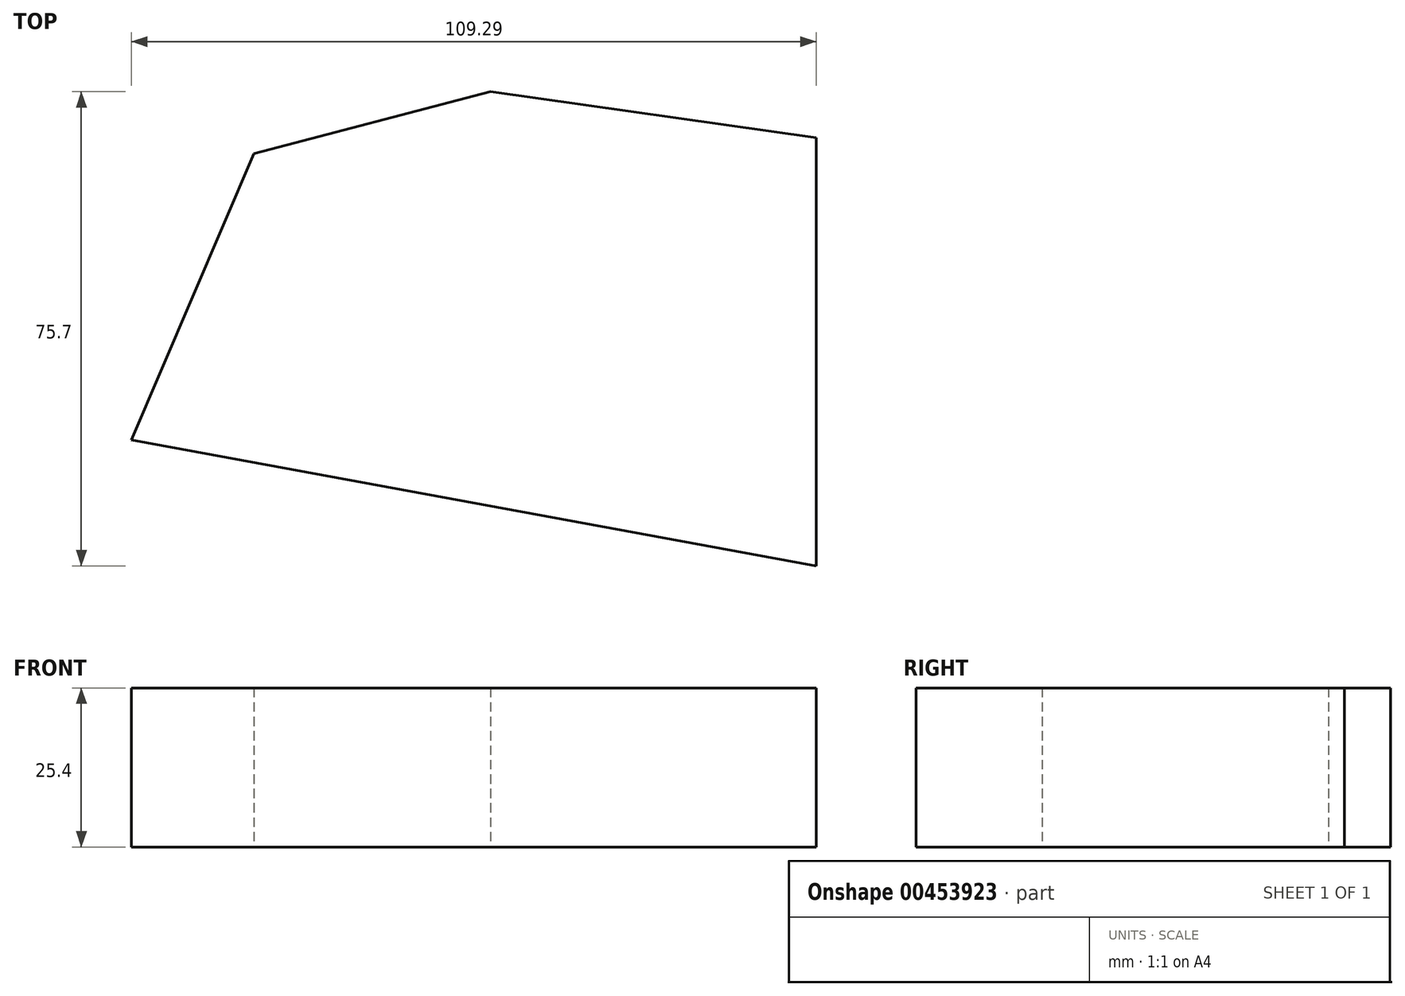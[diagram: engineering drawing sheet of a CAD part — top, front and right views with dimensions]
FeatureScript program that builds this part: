
annotation { "Feature Type Name" : "Feature", "Feature Type Description" : "" }
export const myFeature = defineFeature(function(context is Context, id is Id, definition is map)
    precondition{}
    {
        {
            var Q0;
            Q0=qCreatedBy(makeId("Top.planeOp"),FACE);
            var sketch = newSketch(context, id + "F0", { "sketchPlane" : qUnion([Q0])});
            skLineSegment(sketch, "E0", {"start": v(-59.16, -31) * mm, "end": v(-37.76, 19.1) * mm});
            skLineSegment(sketch, "E1", {"start": v(-37.76, 19.1) * mm, "end": v(0, 28.95) * mm});
            skLineSegment(sketch, "E2", {"start": v(0, 28.95) * mm, "end": v(52, 21.63) * mm});
            skLineSegment(sketch, "E3", {"start": v(52, 21.63) * mm, "end": v(52, -46.75) * mm});
            skLineSegment(sketch, "E4", {"start": v(52, -46.75) * mm, "end": v(-57.3, -26.67) * mm});
            skSolve(sketch);
        }
        {
            var Q0;
            {var subQ0=sQuery(id+"F0.wireOp",EDGE,"E1");Q0=makeQuery(id+"F0.imprint","IMPRINT",FACE,{"disambiguationData":[TD([[makeQuery(id+"F0.imprint","IMPRINT",EDGE,{"derivedFrom":subQ0}),-1.0]])]});}
            extrude(context, id + "F1", {"entities" : qUnion([Q0]), "depth" : 25.4 * mm});
        }
    });
